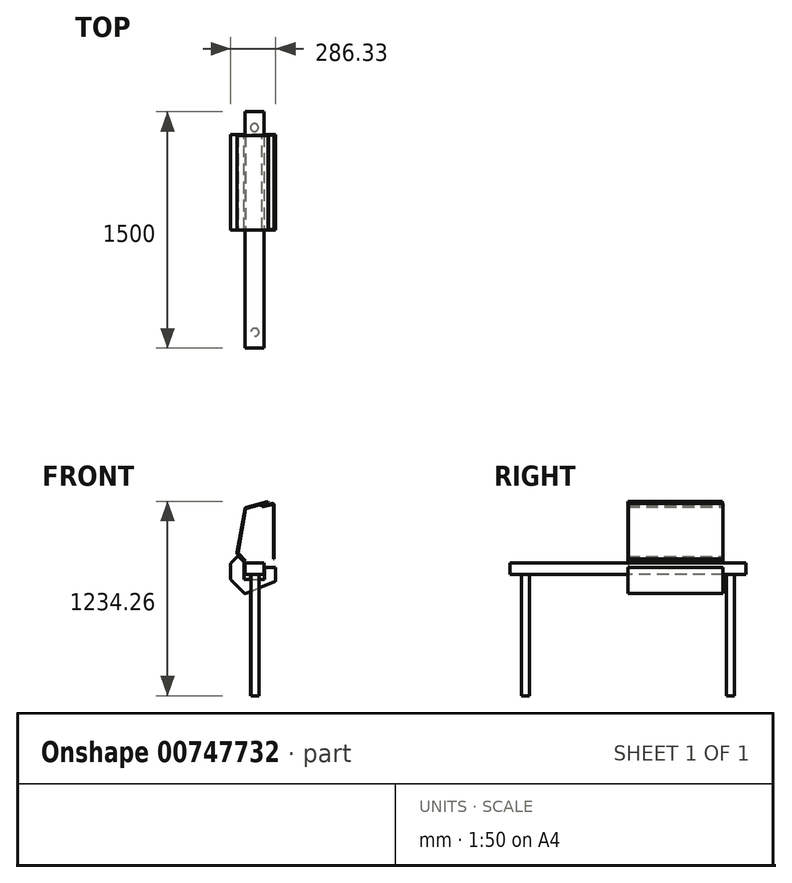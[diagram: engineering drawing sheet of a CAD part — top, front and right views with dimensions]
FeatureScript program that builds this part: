
annotation { "Feature Type Name" : "Feature", "Feature Type Description" : "" }
export const myFeature = defineFeature(function(context is Context, id is Id, definition is map)
    precondition{}
    {
        {
            var Q0;
            Q0=qCreatedBy(makeId("Front.planeOp"),FACE);
            var sketch = newSketch(context, id + "F0", { "sketchPlane" : qUnion([Q0])});
            skLineSegment(sketch, "E0", {"start": v(0, 2.07) * mm, "end": v(0, 97.93) * mm});
            skLineSegment(sketch, "E1", {"start": v(1.46, 101.46) * mm, "end": v(41.46, 141.46) * mm});
            skLineSegment(sketch, "E2", {"start": v(1.46, -1.46) * mm, "end": v(87.82, -87.82) * mm});
            skLineSegment(sketch, "E3", {"start": v(48.54, 141.46) * mm, "end": v(82.33, 107.67) * mm});
            skLineSegment(sketch, "E4", {"start": v(93.26, -88.91) * mm, "end": v(279.23, -12.34) * mm});
            skLineSegment(sketch, "E5", {"start": v(282.33, -7.72) * mm, "end": v(282.33, 75.16) * mm});
            skPoint(sketch, "E6.visualSharp", {"position": v(45, 145) * mm});
            skArc(sketch, "E6.filletArc", {"start": v(48.54, 141.46) * mm, "mid": v(45, 142.93) * mm, "end": v(41.46, 141.46) * mm});
            skPoint(sketch, "E7.visualSharp", {"position": v(0, 100) * mm});
            skArc(sketch, "E7.filletArc", {"start": v(1.46, 101.46) * mm, "mid": v(0.38, 99.84) * mm, "end": v(0, 97.93) * mm});
            skPoint(sketch, "E8.visualSharp", {"position": v(0, 0) * mm});
            skArc(sketch, "E8.filletArc", {"start": v(0, 2.07) * mm, "mid": v(0.38, 0.16) * mm, "end": v(1.46, -1.46) * mm});
            skPoint(sketch, "E9.visualSharp", {"position": v(90.18, -90.18) * mm});
            skArc(sketch, "E9.filletArc", {"start": v(87.82, -87.82) * mm, "mid": v(90.38, -89.19) * mm, "end": v(93.26, -88.91) * mm});
            skPoint(sketch, "E10.visualSharp", {"position": v(282.33, -11.07) * mm});
            skArc(sketch, "E10.filletArc", {"start": v(279.23, -12.34) * mm, "mid": v(281.48, -10.5) * mm, "end": v(282.33, -7.72) * mm});
            skLineSegment(sketch, "E11.0", {"start": v(284.33, -7.72) * mm, "end": v(284.33, 75.16) * mm});
            skArc(sketch, "E11.1", {"start": v(280, -14.2) * mm, "mid": v(283.15, -11.61) * mm, "end": v(284.33, -7.72) * mm});
            skArc(sketch, "E11.2", {"start": v(-2, 2.07) * mm, "mid": v(-1.47, -0.6) * mm, "end": v(0.05, -2.88) * mm});
            skLineSegment(sketch, "E11.3", {"start": v(0.05, -2.88) * mm, "end": v(86.4, -89.24) * mm});
            skArc(sketch, "E11.4", {"start": v(86.4, -89.24) * mm, "mid": v(89.99, -91.15) * mm, "end": v(94.02, -90.76) * mm});
            skLineSegment(sketch, "E11.5", {"start": v(94.02, -90.76) * mm, "end": v(280, -14.2) * mm});
            skLineSegment(sketch, "E12.0", {"start": v(49.95, 142.88) * mm, "end": v(83.74, 109.08) * mm});
            skLineSegment(sketch, "E12.1", {"start": v(-2, 2.07) * mm, "end": v(-2, 97.93) * mm});
            skArc(sketch, "E12.2", {"start": v(0.05, 102.88) * mm, "mid": v(-1.47, 100.6) * mm, "end": v(-2, 97.93) * mm});
            skLineSegment(sketch, "E12.3", {"start": v(0.05, 102.88) * mm, "end": v(40.05, 142.88) * mm});
            skArc(sketch, "E12.4", {"start": v(49.95, 142.88) * mm, "mid": v(45, 144.93) * mm, "end": v(40.05, 142.88) * mm});
            skLineSegment(sketch, "E13", {"start": v(83.74, 109.08) * mm, "end": v(82.33, 107.67) * mm});
            skLineSegment(sketch, "E14", {"start": v(282.33, 75.16) * mm, "end": v(284.33, 75.16) * mm});
            skSolve(sketch);
        }
        {
            var Q0;
            Q0 = qSketchRegion(id + "F0", true);
            extrude(context, id + "F1", {"entities" : qUnion([Q0]), "depth" : 600 * mm, "offsetDistance" : 25 * mm});
        }
        {
            var Q0;
            Q0=makeQuery(id+"F1.opExtrude","CAP_FACE",FACE,{"disambiguationData":[OSD([sQuery(id+"F0.wireOp",EDGE,"E0"),sQuery(id+"F0.wireOp",EDGE,"E1"),sQuery(id+"F0.wireOp",EDGE,"E2"),sQuery(id+"F0.wireOp",EDGE,"E3"),sQuery(id+"F0.wireOp",EDGE,"E4"),sQuery(id+"F0.wireOp",EDGE,"E5"),sQuery(id+"F0.wireOp",EDGE,"E6.filletArc"),sQuery(id+"F0.wireOp",EDGE,"E7.filletArc"),sQuery(id+"F0.wireOp",EDGE,"E8.filletArc"),sQuery(id+"F0.wireOp",EDGE,"E9.filletArc"),sQuery(id+"F0.wireOp",EDGE,"E10.filletArc"),sQuery(id+"F0.wireOp",EDGE,"E11.0"),sQuery(id+"F0.wireOp",EDGE,"E11.1"),sQuery(id+"F0.wireOp",EDGE,"E11.2"),sQuery(id+"F0.wireOp",EDGE,"E11.3"),sQuery(id+"F0.wireOp",EDGE,"E11.4"),sQuery(id+"F0.wireOp",EDGE,"E11.5"),sQuery(id+"F0.wireOp",EDGE,"E12.0"),sQuery(id+"F0.wireOp",EDGE,"E12.1"),sQuery(id+"F0.wireOp",EDGE,"E12.2"),sQuery(id+"F0.wireOp",EDGE,"E12.3"),sQuery(id+"F0.wireOp",EDGE,"E12.4"),sQuery(id+"F0.wireOp",EDGE,"E13"),sQuery(id+"F0.wireOp",EDGE,"E14")])],"isStart":false});
            var sketch = newSketch(context, id + "F2", { "sketchPlane" : qUnion([Q0])});
            skLineSegment(sketch, "E15.0", {"start": v(49.95, 142.88) * mm, "end": v(83.74, 109.08) * mm});
            skPoint(sketch, "E16.0", {"position": v(40.05, 142.88) * mm});
            skLineSegment(sketch, "E17.0", {"start": v(0.05, 102.88) * mm, "end": v(40.05, 142.88) * mm});
            skPoint(sketch, "E18.0", {"position": v(48.54, 141.46) * mm});
            skArc(sketch, "E19.0", {"start": v(49.95, 142.88) * mm, "mid": v(45, 144.93) * mm, "end": v(40.05, 142.88) * mm});
            skArc(sketch, "E20.0", {"start": v(0.05, 102.88) * mm, "mid": v(-1.47, 100.6) * mm, "end": v(-2, 97.93) * mm});
            skLineSegment(sketch, "E21.0", {"start": v(-2, 2.07) * mm, "end": v(-2, 97.93) * mm});
            skPoint(sketch, "E22.0", {"position": v(0.05, -2.88) * mm});
            skArc(sketch, "E23.0", {"start": v(-2, 2.07) * mm, "mid": v(-1.47, -0.6) * mm, "end": v(0.05, -2.88) * mm});
            skLineSegment(sketch, "E24.0", {"start": v(0.05, -2.88) * mm, "end": v(86.4, -89.24) * mm});
            skArc(sketch, "E25.0", {"start": v(86.4, -89.24) * mm, "mid": v(89.99, -91.15) * mm, "end": v(94.02, -90.76) * mm});
            skLineSegment(sketch, "E26.0", {"start": v(94.02, -90.76) * mm, "end": v(280, -14.2) * mm});
            skArc(sketch, "E27.0", {"start": v(280, -14.2) * mm, "mid": v(283.15, -11.61) * mm, "end": v(284.33, -7.72) * mm});
            skLineSegment(sketch, "E28.0", {"start": v(284.33, -7.72) * mm, "end": v(284.33, 75.16) * mm});
            skLineSegment(sketch, "E29", {"start": v(83.74, 109.08) * mm, "end": v(83.74, 0) * mm});
            skLineSegment(sketch, "E30", {"start": v(83.74, 0) * mm, "end": v(213.74, 0) * mm});
            skLineSegment(sketch, "E31", {"start": v(213.74, 0) * mm, "end": v(213.74, 75.16) * mm});
            skLineSegment(sketch, "E32", {"start": v(213.74, 75.16) * mm, "end": v(284.33, 75.16) * mm});
            skSolve(sketch);
        }
        {
            var Q0;
            Q0 = qSketchRegion(id + "F2", true);
            extrude(context, id + "F3", {"entities" : qUnion([Q0]), "operationType" : NewBodyOperationType.ADD, "depth" : 2 * mm, "offsetDistance" : 25 * mm});
        }
        {
            var Q0;
            Q0=makeQuery(id+"F1.opExtrude","CAP_FACE",FACE,{"disambiguationData":[OSD([sQuery(id+"F0.wireOp",EDGE,"E0"),sQuery(id+"F0.wireOp",EDGE,"E1"),sQuery(id+"F0.wireOp",EDGE,"E2"),sQuery(id+"F0.wireOp",EDGE,"E3"),sQuery(id+"F0.wireOp",EDGE,"E4"),sQuery(id+"F0.wireOp",EDGE,"E5"),sQuery(id+"F0.wireOp",EDGE,"E6.filletArc"),sQuery(id+"F0.wireOp",EDGE,"E7.filletArc"),sQuery(id+"F0.wireOp",EDGE,"E8.filletArc"),sQuery(id+"F0.wireOp",EDGE,"E9.filletArc"),sQuery(id+"F0.wireOp",EDGE,"E10.filletArc"),sQuery(id+"F0.wireOp",EDGE,"E11.0"),sQuery(id+"F0.wireOp",EDGE,"E11.1"),sQuery(id+"F0.wireOp",EDGE,"E11.2"),sQuery(id+"F0.wireOp",EDGE,"E11.3"),sQuery(id+"F0.wireOp",EDGE,"E11.4"),sQuery(id+"F0.wireOp",EDGE,"E11.5"),sQuery(id+"F0.wireOp",EDGE,"E12.0"),sQuery(id+"F0.wireOp",EDGE,"E12.1"),sQuery(id+"F0.wireOp",EDGE,"E12.2"),sQuery(id+"F0.wireOp",EDGE,"E12.3"),sQuery(id+"F0.wireOp",EDGE,"E12.4"),sQuery(id+"F0.wireOp",EDGE,"E13"),sQuery(id+"F0.wireOp",EDGE,"E14")])],"isStart":true});
            var sketch = newSketch(context, id + "F4", { "sketchPlane" : qUnion([Q0])});
            skLineSegment(sketch, "E33.0.0", {"start": v(-284.33, 75.16) * mm, "end": v(-213.74, 75.16) * mm});
            skLineSegment(sketch, "E33.0.1", {"start": v(-213.74, 75.16) * mm, "end": v(-213.74, 0) * mm});
            skLineSegment(sketch, "E33.0.2", {"start": v(-213.74, 0) * mm, "end": v(-83.74, 0) * mm});
            skLineSegment(sketch, "E33.0.3", {"start": v(-83.74, 0) * mm, "end": v(-83.74, 109.08) * mm});
            skLineSegment(sketch, "E33.0.4", {"start": v(-83.74, 109.08) * mm, "end": v(-49.95, 142.88) * mm});
            skArc(sketch, "E33.0.5", {"start": v(-49.95, 142.88) * mm, "mid": v(-45, 144.93) * mm, "end": v(-40.05, 142.88) * mm});
            skLineSegment(sketch, "E33.0.6", {"start": v(-40.05, 142.88) * mm, "end": v(-0.05, 102.88) * mm});
            skArc(sketch, "E33.0.7", {"start": v(-0.05, 102.88) * mm, "mid": v(1.47, 100.6) * mm, "end": v(2, 97.93) * mm});
            skLineSegment(sketch, "E33.0.8", {"start": v(2, 97.93) * mm, "end": v(2, 2.07) * mm});
            skArc(sketch, "E33.0.9", {"start": v(2, 2.07) * mm, "mid": v(1.47, -0.6) * mm, "end": v(-0.05, -2.88) * mm});
            skLineSegment(sketch, "E33.0.10", {"start": v(-0.05, -2.88) * mm, "end": v(-86.4, -89.24) * mm});
            skArc(sketch, "E33.0.11", {"start": v(-86.4, -89.24) * mm, "mid": v(-89.99, -91.15) * mm, "end": v(-94.02, -90.76) * mm});
            skLineSegment(sketch, "E33.0.12", {"start": v(-94.02, -90.76) * mm, "end": v(-280, -14.2) * mm});
            skArc(sketch, "E33.0.13", {"start": v(-280, -14.2) * mm, "mid": v(-283.15, -11.61) * mm, "end": v(-284.33, -7.72) * mm});
            skLineSegment(sketch, "E33.0.14", {"start": v(-284.33, -7.72) * mm, "end": v(-284.33, 75.16) * mm});
            skSolve(sketch);
        }
        {
            var Q0;
            Q0 = qSketchRegion(id + "F4", true);
            extrude(context, id + "F5", {"entities" : qUnion([Q0]), "operationType" : NewBodyOperationType.ADD, "depth" : 2 * mm, "offsetDistance" : 25 * mm});
        }
        {
            var Q0;
            Q0=makeQuery(id+"F3.opExtrude","CAP_FACE",FACE,{"disambiguationData":[OSD([sQuery(id+"F2.wireOp",EDGE,"E15.0"),sQuery(id+"F2.wireOp",EDGE,"E17.0"),sQuery(id+"F2.wireOp",EDGE,"E19.0"),sQuery(id+"F2.wireOp",EDGE,"E20.0"),sQuery(id+"F2.wireOp",EDGE,"E21.0"),sQuery(id+"F2.wireOp",EDGE,"E23.0"),sQuery(id+"F2.wireOp",EDGE,"E24.0"),sQuery(id+"F2.wireOp",EDGE,"E25.0"),sQuery(id+"F2.wireOp",EDGE,"E26.0"),sQuery(id+"F2.wireOp",EDGE,"E27.0"),sQuery(id+"F2.wireOp",EDGE,"E28.0"),sQuery(id+"F2.wireOp",EDGE,"E29"),sQuery(id+"F2.wireOp",EDGE,"E30"),sQuery(id+"F2.wireOp",EDGE,"E31"),sQuery(id+"F2.wireOp",EDGE,"E32")])],"isStart":false});
            var sketch = newSketch(context, id + "F6", { "sketchPlane" : qUnion([Q0])});
            skLineSegment(sketch, "E34", {"start": v(92.1, 117.19) * mm, "end": v(46.58, 162.7) * mm});
            skLineSegment(sketch, "E35", {"start": v(44.92, 167.98) * mm, "end": v(93.98, 446.24) * mm});
            skLineSegment(sketch, "E36", {"start": v(98.34, 450.99) * mm, "end": v(238.19, 488.46) * mm});
            skPoint(sketch, "E37.visualSharp", {"position": v(94.64, 450) * mm});
            skArc(sketch, "E37.filletArc", {"start": v(98.34, 450.99) * mm, "mid": v(95.47, 449.25) * mm, "end": v(93.98, 446.24) * mm});
            skPoint(sketch, "E38.visualSharp", {"position": v(44.37, 164.9) * mm});
            skArc(sketch, "E38.filletArc", {"start": v(44.92, 167.98) * mm, "mid": v(45.1, 165.13) * mm, "end": v(46.58, 162.7) * mm});
            skLineSegment(sketch, "E39.0", {"start": v(96.78, 456.78) * mm, "end": v(236.64, 494.26) * mm});
            skLineSegment(sketch, "E39.1", {"start": v(87.85, 112.95) * mm, "end": v(42.34, 158.45) * mm});
            skArc(sketch, "E39.2", {"start": v(39, 169.02) * mm, "mid": v(39.38, 163.33) * mm, "end": v(42.34, 158.45) * mm});
            skLineSegment(sketch, "E39.3", {"start": v(39, 169.02) * mm, "end": v(88.07, 447.28) * mm});
            skArc(sketch, "E39.4", {"start": v(96.78, 456.78) * mm, "mid": v(91.04, 453.3) * mm, "end": v(88.07, 447.28) * mm});
            skLineSegment(sketch, "E40", {"start": v(87.85, 112.95) * mm, "end": v(92.1, 117.19) * mm});
            skLineSegment(sketch, "E41", {"start": v(236.64, 494.26) * mm, "end": v(238.19, 488.46) * mm});
            skSolve(sketch);
        }
        {
            var Q0;
            Q0 = qSketchRegion(id + "F6", true);
            extrude(context, id + "F7", {"entities" : qUnion([Q0]), "oppositeDirection" : true, "depth" : 600 * mm, "offsetDistance" : 25 * mm});
        }
        {
            var Q0;
            Q0=makeQuery(id+"F3.opExtrude","CAP_FACE",FACE,{"disambiguationData":[OSD([sQuery(id+"F2.wireOp",EDGE,"E15.0"),sQuery(id+"F2.wireOp",EDGE,"E17.0"),sQuery(id+"F2.wireOp",EDGE,"E19.0"),sQuery(id+"F2.wireOp",EDGE,"E20.0"),sQuery(id+"F2.wireOp",EDGE,"E21.0"),sQuery(id+"F2.wireOp",EDGE,"E23.0"),sQuery(id+"F2.wireOp",EDGE,"E24.0"),sQuery(id+"F2.wireOp",EDGE,"E25.0"),sQuery(id+"F2.wireOp",EDGE,"E26.0"),sQuery(id+"F2.wireOp",EDGE,"E27.0"),sQuery(id+"F2.wireOp",EDGE,"E28.0"),sQuery(id+"F2.wireOp",EDGE,"E29"),sQuery(id+"F2.wireOp",EDGE,"E30"),sQuery(id+"F2.wireOp",EDGE,"E31"),sQuery(id+"F2.wireOp",EDGE,"E32")])],"isStart":false});
            var sketch = newSketch(context, id + "F8", { "sketchPlane" : qUnion([Q0])});
            skLineSegment(sketch, "E42.bottom", {"start": v(209.7, 105) * mm, "end": v(89.7, 105) * mm});
            skLineSegment(sketch, "E42.top", {"start": v(209.7, 30) * mm, "end": v(89.7, 30) * mm});
            skLineSegment(sketch, "E42.left", {"start": v(209.7, 105) * mm, "end": v(209.7, 30) * mm});
            skLineSegment(sketch, "E42.right", {"start": v(89.7, 105) * mm, "end": v(89.7, 30) * mm});
            skPoint(sketch, "E42.middle", {"position": v(149.7, 67.5) * mm});
            skSolve(sketch);
        }
        {
            var Q0;
            Q0 = qSketchRegion(id + "F8", true);
            extrude(context, id + "F9", {"entities" : qUnion([Q0]), "endBound" : BoundingType.SYMMETRIC, "oppositeDirection" : true, "depth" : 1500 * mm, "offsetDistance" : 25 * mm});
        }
        {
            var Q0;
            Q0=makeQuery(id+"F3.opExtrude","CAP_FACE",FACE,{"disambiguationData":[OSD([sQuery(id+"F2.wireOp",EDGE,"E15.0"),sQuery(id+"F2.wireOp",EDGE,"E17.0"),sQuery(id+"F2.wireOp",EDGE,"E19.0"),sQuery(id+"F2.wireOp",EDGE,"E20.0"),sQuery(id+"F2.wireOp",EDGE,"E21.0"),sQuery(id+"F2.wireOp",EDGE,"E23.0"),sQuery(id+"F2.wireOp",EDGE,"E24.0"),sQuery(id+"F2.wireOp",EDGE,"E25.0"),sQuery(id+"F2.wireOp",EDGE,"E26.0"),sQuery(id+"F2.wireOp",EDGE,"E27.0"),sQuery(id+"F2.wireOp",EDGE,"E28.0"),sQuery(id+"F2.wireOp",EDGE,"E29"),sQuery(id+"F2.wireOp",EDGE,"E30"),sQuery(id+"F2.wireOp",EDGE,"E31"),sQuery(id+"F2.wireOp",EDGE,"E32")])],"isStart":false});
            var Q1;
            Q1=makeQuery(id+"F5.opExtrude","CAP_FACE",FACE,{"disambiguationData":[OSD([sQuery(id+"F4.wireOp",EDGE,"E33.0.0"),sQuery(id+"F4.wireOp",EDGE,"E33.0.1"),sQuery(id+"F4.wireOp",EDGE,"E33.0.2"),sQuery(id+"F4.wireOp",EDGE,"E33.0.3"),sQuery(id+"F4.wireOp",EDGE,"E33.0.4"),sQuery(id+"F4.wireOp",EDGE,"E33.0.5"),sQuery(id+"F4.wireOp",EDGE,"E33.0.6"),sQuery(id+"F4.wireOp",EDGE,"E33.0.7"),sQuery(id+"F4.wireOp",EDGE,"E33.0.8"),sQuery(id+"F4.wireOp",EDGE,"E33.0.9"),sQuery(id+"F4.wireOp",EDGE,"E33.0.10"),sQuery(id+"F4.wireOp",EDGE,"E33.0.11"),sQuery(id+"F4.wireOp",EDGE,"E33.0.12"),sQuery(id+"F4.wireOp",EDGE,"E33.0.13"),sQuery(id+"F4.wireOp",EDGE,"E33.0.14")])],"isStart":false});
            cPlane(context, id + "F10", {"entities" : qUnion([Q0, Q1]), "cplaneType" : CPlaneType.MID_PLANE, "offset" : 25 * mm, "oppositeDirection" : true, "width" : 150 * mm, "height" : 150 * mm});
        }
        {
            var Q0;
            Q0=qCreatedBy(id+"F10.planeOp",FACE);
            var sketch = newSketch(context, id + "F11", { "sketchPlane" : qUnion([Q0])});
            skLineSegment(sketch, "E43", {"start": v(197.59, 463.36) * mm, "end": v(261.47, 480.47) * mm});
            skLineSegment(sketch, "E44", {"start": v(274.06, 470.81) * mm, "end": v(274.06, 128.41) * mm});
            skLineSegment(sketch, "E45.0", {"start": v(269.06, 470.81) * mm, "end": v(269.06, 128.41) * mm});
            skLineSegment(sketch, "E45.1", {"start": v(198.88, 458.53) * mm, "end": v(262.76, 475.64) * mm});
            skLineSegment(sketch, "E46", {"start": v(197.59, 463.36) * mm, "end": v(198.88, 458.53) * mm});
            skLineSegment(sketch, "E47", {"start": v(269.06, 128.41) * mm, "end": v(274.06, 128.41) * mm});
            skPoint(sketch, "E48.visualSharp", {"position": v(269.06, 477.33) * mm});
            skArc(sketch, "E48.filletArc", {"start": v(269.06, 470.81) * mm, "mid": v(267.1, 474.78) * mm, "end": v(262.76, 475.64) * mm});
            skPoint(sketch, "E49.visualSharp", {"position": v(274.06, 483.85) * mm});
            skArc(sketch, "E49.filletArc", {"start": v(274.06, 470.81) * mm, "mid": v(270.14, 478.75) * mm, "end": v(261.47, 480.47) * mm});
            skSolve(sketch);
        }
        {
            var Q0;
            Q0 = qSketchRegion(id + "F11", true);
            extrude(context, id + "F12", {"entities" : qUnion([Q0]), "endBound" : BoundingType.SYMMETRIC, "depth" : 600 * mm, "offsetDistance" : 25 * mm});
        }
        {
            var Q0;
            Q0=makeQuery(id+"F9.opExtrude","SWEPT_FACE",FACE,{"disambiguationData":[OSD([sQuery(id+"F8.wireOp",EDGE,"E42.top")])]});
            var sketch = newSketch(context, id + "F13", { "sketchPlane" : qUnion([Q0])});
            skCircle(sketch, "E50", {"center": v(152.68, 1252) * mm, "radius": 25 * mm});
            skCircle(sketch, "E51", {"center": v(149.7, -48) * mm, "radius": 25 * mm});
            skSolve(sketch);
        }
        {
            var Q0;
            Q0=makeQuery(id+"F13.imprint","IMPRINT",FACE,{"disambiguationData":[TD([[makeQuery(id+"F13.imprint","IMPRINT",EDGE,{"derivedFrom":sQuery(id+"F13.wireOp",EDGE,"E50")}),1.0]])]});
            var Q1;
            Q1=makeQuery(id+"F13.imprint","IMPRINT",FACE,{"disambiguationData":[TD([[makeQuery(id+"F13.imprint","IMPRINT",EDGE,{"derivedFrom":sQuery(id+"F13.wireOp",EDGE,"E51")}),1.0]])]});
            extrude(context, id + "F14", {"entities" : qUnion([Q0, Q1]), "operationType" : NewBodyOperationType.ADD, "depth" : 770 * mm, "offsetDistance" : 25 * mm});
        }
    });
